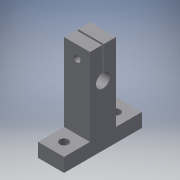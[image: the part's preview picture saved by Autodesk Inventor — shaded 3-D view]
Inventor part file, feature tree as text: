
AUTODESK INVENTOR PART (.ipt)
format: ipt  version: 2019 (Build 230136000, 136)  size: 147,968 bytes
history: native  units: mm
features: extrude x4, sketch x3, projected_geometry x2
ambient origin geometry x8: Origin, YZ Plane, XZ Plane, XY Plane, X Axis, Y Axis, Z Axis, Center Point
bodies: Solid1 (feature_tree)
feature tree (9):
  sketch  "Sketch1"  dims[d0=8.0mm d1=1.0mm]
  extrude  "Extrusion1"  Depth=1.0mm
  extrude  "Extrusion2"  Depth=15.0mm
  extrude  "Extrusion3"  Depth=8.0mm
  extrude  "Extrusion4"  Depth=15.0mm TaperAngle=0.0deg
  sketch  "Sketch2"  dims[d2=7.0mm d3=15.0mm]
  projected_geometry  "Projected Loop1"
  projected_geometry  "Projected Loop2"
  sketch  "Sketch3"  dims[d5=45.0mm d6=8.0mm d7=15.0mm d8=0.0mm d9=10.0mm d10=0.0mm d11=40.0mm d12=5.0mm d13=10.0mm d14=0.0mm d15=4.25mm d16=10.0mm d17=0.0mm]
